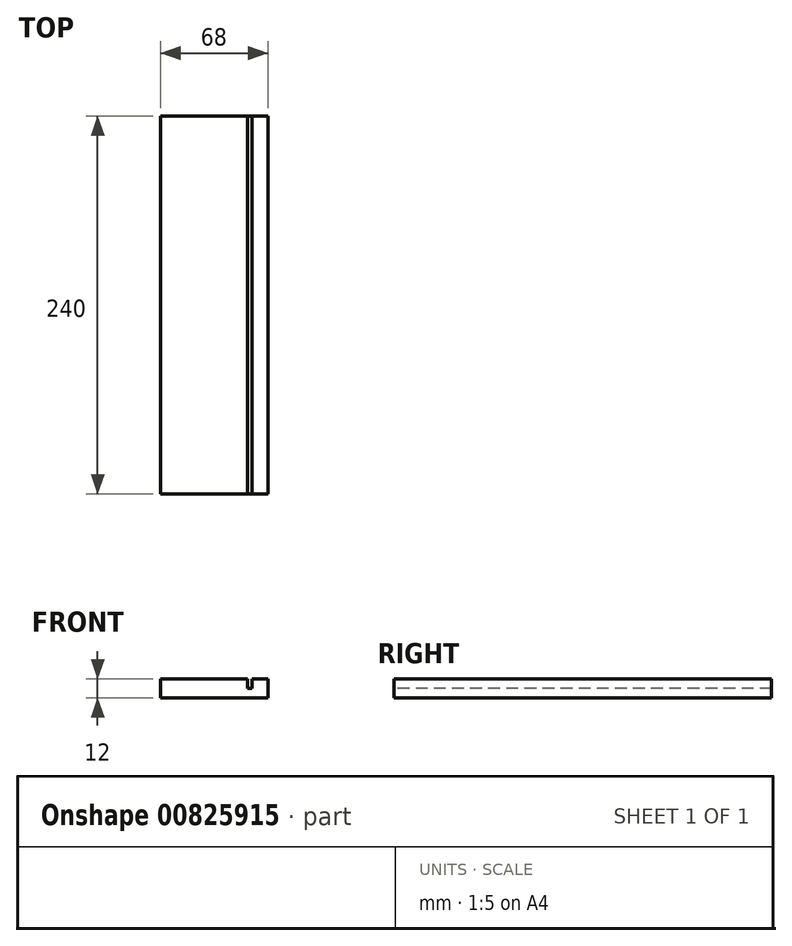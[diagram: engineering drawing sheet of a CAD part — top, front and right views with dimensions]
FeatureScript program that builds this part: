
annotation { "Feature Type Name" : "Feature", "Feature Type Description" : "" }
export const myFeature = defineFeature(function(context is Context, id is Id, definition is map)
    precondition{}
    {
        {
            var Q0;
            Q0=qCreatedBy(makeId("Front.planeOp"),FACE);
            var sketch = newSketch(context, id + "F0", { "sketchPlane" : qUnion([Q0])});
            skLineSegment(sketch, "E0.bottom", {"start": v(-34, 6) * mm, "end": v(34, 6) * mm});
            skLineSegment(sketch, "E0.top", {"start": v(-34, -6) * mm, "end": v(34, -6) * mm});
            skLineSegment(sketch, "E0.left", {"start": v(-34, 6) * mm, "end": v(-34, -6) * mm});
            skLineSegment(sketch, "E0.right", {"start": v(34, 6) * mm, "end": v(34, -6) * mm});
            skPoint(sketch, "E0.middle", {"position": v(0, 0) * mm});
            skPoint(sketch, "E1.endSnap0", {"position": v(-34, 0) * mm});
            skSolve(sketch);
        }
        {
            var Q0;
            Q0 = qSketchRegion(id + "F0", true);
            extrude(context, id + "F1", {"entities" : qUnion([Q0]), "depth" : 240 * mm, "offsetDistance" : 25 * mm});
        }
        {
            var Q0;
            Q0=makeQuery(id+"F1.opExtrude","CAP_FACE",FACE,{"disambiguationData":[OSD([sQuery(id+"F0.wireOp",EDGE,"E0.bottom"),sQuery(id+"F0.wireOp",EDGE,"E0.top"),sQuery(id+"F0.wireOp",EDGE,"E0.left"),sQuery(id+"F0.wireOp",EDGE,"E0.right")])],"isStart":false});
            var sketch = newSketch(context, id + "F2", { "sketchPlane" : qUnion([Q0])});
            skLineSegment(sketch, "E2", {"start": v(21, 6) * mm, "end": v(21, 0) * mm});
            skLineSegment(sketch, "E3", {"start": v(21, 0) * mm, "end": v(24, 0) * mm});
            skLineSegment(sketch, "E4", {"start": v(24, 0) * mm, "end": v(24, 6) * mm});
            skSolve(sketch);
        }
        {
            var Q0;
            {var subQ0=sQuery(id+"F2.wireOp",EDGE,"E2");Q0=makeQuery(id+"F2.imprint","IMPRINT",FACE,{"disambiguationData":[TD([[makeQuery(id+"F2.imprint","IMPRINT",EDGE,{"derivedFrom":subQ0}),1.0]])]});}
            extrude(context, id + "F3", {"entities" : qUnion([Q0]), "operationType" : NewBodyOperationType.REMOVE, "oppositeDirection" : true, "depth" : 340 * mm, "offsetDistance" : 25 * mm});
        }
    });
